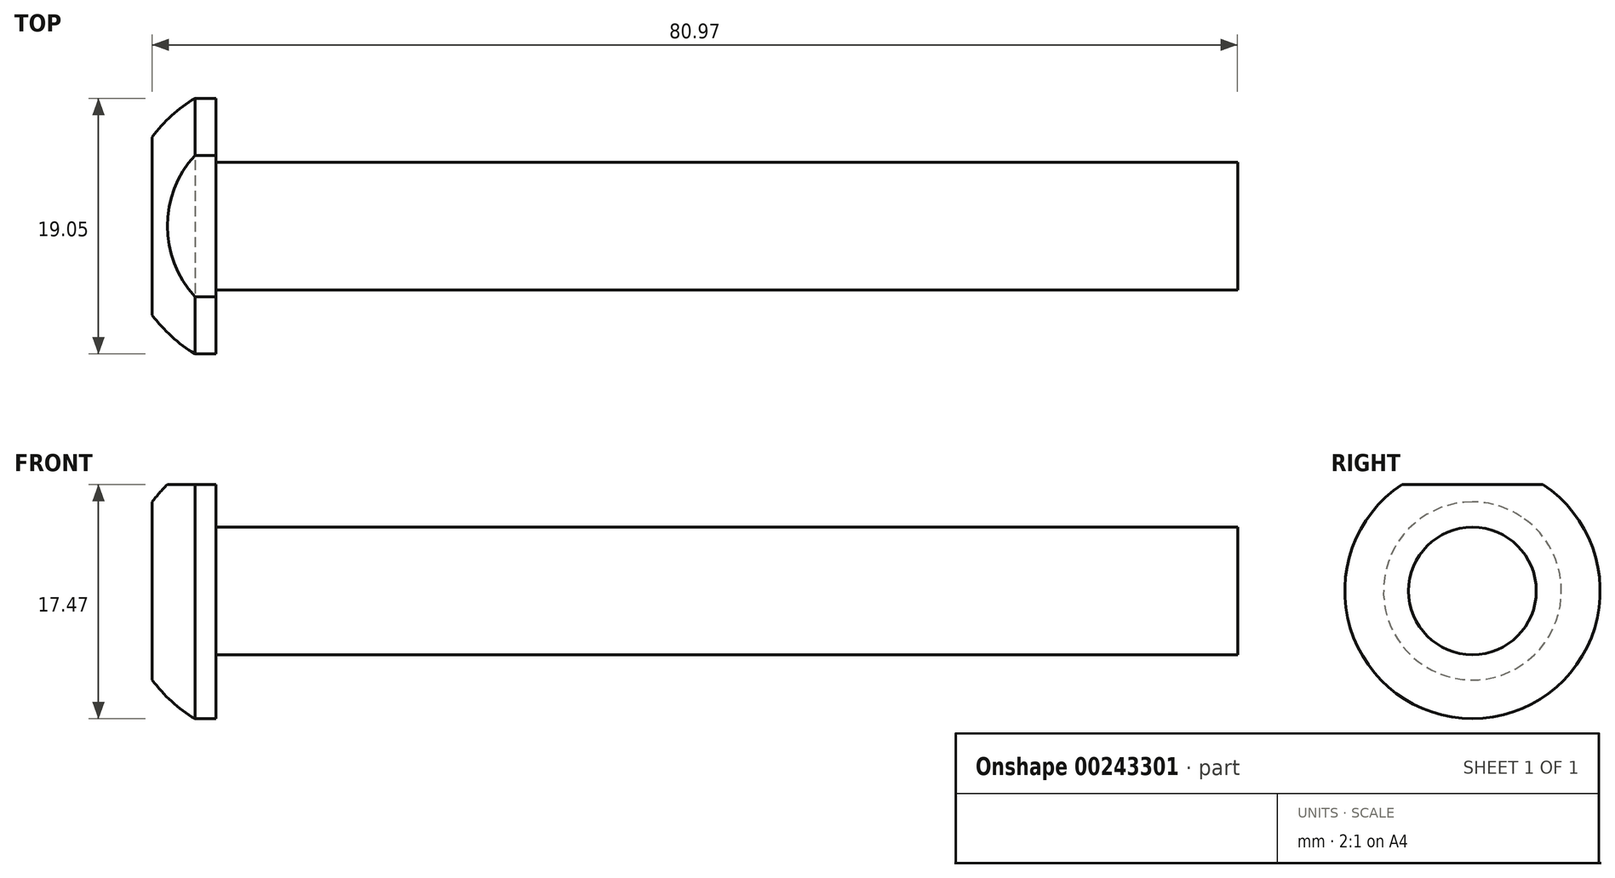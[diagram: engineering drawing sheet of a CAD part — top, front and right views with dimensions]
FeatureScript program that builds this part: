
annotation { "Feature Type Name" : "Feature", "Feature Type Description" : "" }
export const myFeature = defineFeature(function(context is Context, id is Id, definition is map)
    precondition{}
    {
        {
            var Q0;
            Q0=qCreatedBy(makeId("Top.planeOp"),FACE);
            var sketch = newSketch(context, id + "F0", { "sketchPlane" : qUnion([Q0])});
            skLineSegment(sketch, "E0.bottom", {"start": v(0, 9.67) * mm, "end": v(76.21, 9.67) * mm});
            skLineSegment(sketch, "E0.top", {"start": v(0, 14.43) * mm, "end": v(76.21, 14.43) * mm});
            skLineSegment(sketch, "E0.right", {"start": v(76.21, 9.67) * mm, "end": v(76.21, 14.43) * mm});
            skLineSegment(sketch, "E1", {"start": v(0, 14.43) * mm, "end": v(0, 19.2) * mm});
            skLineSegment(sketch, "E2", {"start": v(0, 19.2) * mm, "end": v(-1.57, 19.2) * mm});
            skArc(sketch, "E3", {"start": v(-1.57, 19.2) * mm, "mid": v(-3.3, 17.9) * mm, "end": v(-4.76, 16.3) * mm});
            skLineSegment(sketch, "E4", {"start": v(0, 9.67) * mm, "end": v(-4.76, 9.67) * mm});
            skLineSegment(sketch, "E5", {"start": v(-4.76, 9.67) * mm, "end": v(-4.76, 16.3) * mm});
            skSolve(sketch);
        }
        {
            var Q0;
            Q0=makeQuery(id+"F0.imprint","IMPRINT",FACE,{"disambiguationData":[TD([[makeQuery(id+"F0.imprint","IMPRINT",EDGE,{"derivedFrom":sQuery(id+"F0.wireOp",EDGE,"E0.bottom")}),1.0]])]});
            var Q1;
            Q1=sQuery(id+"F0.wireOp",EDGE,"E0.bottom");
            revolve(context, id + "F1", {"entities" : qUnion([Q0]), "axis" : qUnion([Q1]), "revolveType" : RevolveType.FULL});
        }
        {
            var Q0;
            Q0=makeQuery(id+"F1.opRevolve","SWEPT_FACE",FACE,{"disambiguationData":[OSD([sQuery(id+"F0.wireOp",EDGE,"E5")])]});
            var sketch = newSketch(context, id + "F2", { "sketchPlane" : qUnion([Q0])});
            skLineSegment(sketch, "E6.top", {"start": v(-22.37, 14.37) * mm, "end": v(2.33, 14.37) * mm});
            skLineSegment(sketch, "E6.left", {"start": v(-22.37, 7.94) * mm, "end": v(-22.37, 14.37) * mm});
            skLineSegment(sketch, "E6.right", {"start": v(2.33, 7.94) * mm, "end": v(2.33, 14.37) * mm});
            skPoint(sketch, "E7.start.orphan", {"position": v(-9.67, 0) * mm});
            skLineSegment(sketch, "E8", {"start": v(2.33, 7.94) * mm, "end": v(-22.37, 7.94) * mm});
            skSolve(sketch);
        }
        {
            var Q0;
            Q0 = qSketchRegion(id + "F2", true);
            extrude(context, id + "F3", {"entities" : qUnion([Q0]), "operationType" : NewBodyOperationType.REMOVE, "oppositeDirection" : true, "depth" : 25.4 * mm});
        }
    });
